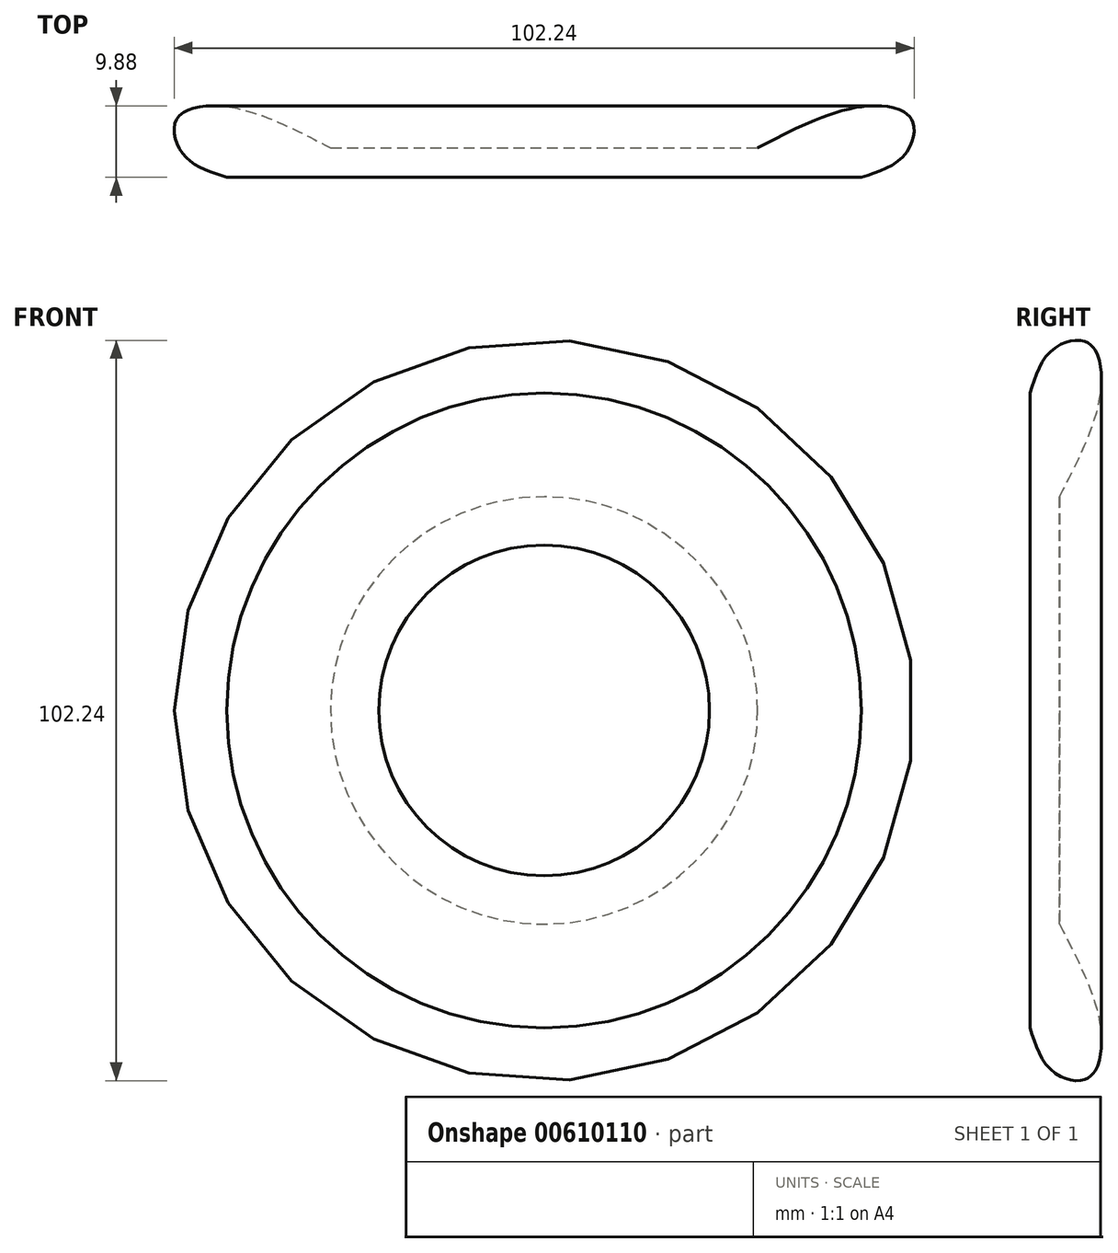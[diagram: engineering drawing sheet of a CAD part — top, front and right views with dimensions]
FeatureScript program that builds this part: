
annotation { "Feature Type Name" : "Feature", "Feature Type Description" : "" }
export const myFeature = defineFeature(function(context is Context, id is Id, definition is map)
    precondition{}
    {
        {
            var Q0;
            Q0=qCreatedBy(makeId("Top.planeOp"),FACE);
            var sketch = newSketch(context, id + "F0", { "sketchPlane" : qUnion([Q0])});
            skLineSegment(sketch, "E0", {"start": v(-22.84, 0) * mm, "end": v(-43.84, 0) * mm});
            skFitSpline(sketch, "E1", {"points": [v(-43.84, 0) * mm, v(-49.76, 3.09) * mm, v(-50.75, 8.03) * mm, v(-43.84, 9.76) * mm, v(-29.51, 4.07) * mm], "startDerivative": vector(-30, 9.5) * mm, "endDerivative": vector(42.82, -22.24) * mm});
            skSolve(sketch);
        }
        {
            var Q0;
            Q0=qCreatedBy(makeId("Front.planeOp"),FACE);
            var sketch = newSketch(context, id + "F1", { "sketchPlane" : qUnion([Q0])});
            skCircle(sketch, "E2", {"center": v(0, 0) * mm, "radius": 22.6 * mm});
            skSolve(sketch);
        }
        {
            var Q0;
            Q0 = qSketchRegion(id + "F0", true);
            var Q1;
            Q1=sQuery(id+"F0.wireOp",EDGE,"E1");
            var Q2;
            Q2=sQuery(id+"F0.wireOp",EDGE,"E0");
            var Q3;
            Q3=sQuery(id+"F1.wireOp",EDGE,"E2");
            sweep(context, id + "F2", {"bodyType" : ToolBodyType.SURFACE, "profiles" : qUnion([Q0]), "surfaceProfiles" : qUnion([Q1, Q2]), "path" : qUnion([Q3])});
        }
        {
            var Q0;
            Q0=qCreatedBy(makeId("Right.planeOp"),FACE);
            var sketch = newSketch(context, id + "F3", { "sketchPlane" : qUnion([Q0])});
            skFitSpline(sketch, "E3", {"points": [v(5.66, 32.8) * mm, v(12, 44.22) * mm, v(28.4, 60.63) * mm, v(33.49, 64.06) * mm], "startDerivative": vector(13.7, 32.12) * mm, "endDerivative": vector(18.68, 10.81) * mm});
            skLineSegment(sketch, "E4", {"start": v(0, 68.86) * mm, "end": v(33.58, 68.86) * mm});
            skLineSegment(sketch, "E5", {"start": v(33.58, 68.86) * mm, "end": v(33.49, 64.06) * mm});
            skLineSegment(sketch, "E6", {"start": v(0, 68.86) * mm, "end": v(0, 27.99) * mm});
            skSolve(sketch);
        }
        {
            var Q0;
            Q0=qCreatedBy(makeId("Front.planeOp"),FACE);
            var sketch = newSketch(context, id + "F4", { "sketchPlane" : qUnion([Q0])});
            skArc(sketch, "E7", {"start": v(-25.49, 63.92) * mm, "mid": v(-0.09, 68.81) * mm, "end": v(25.32, 63.98) * mm});
            skSolve(sketch);
        }
    });
